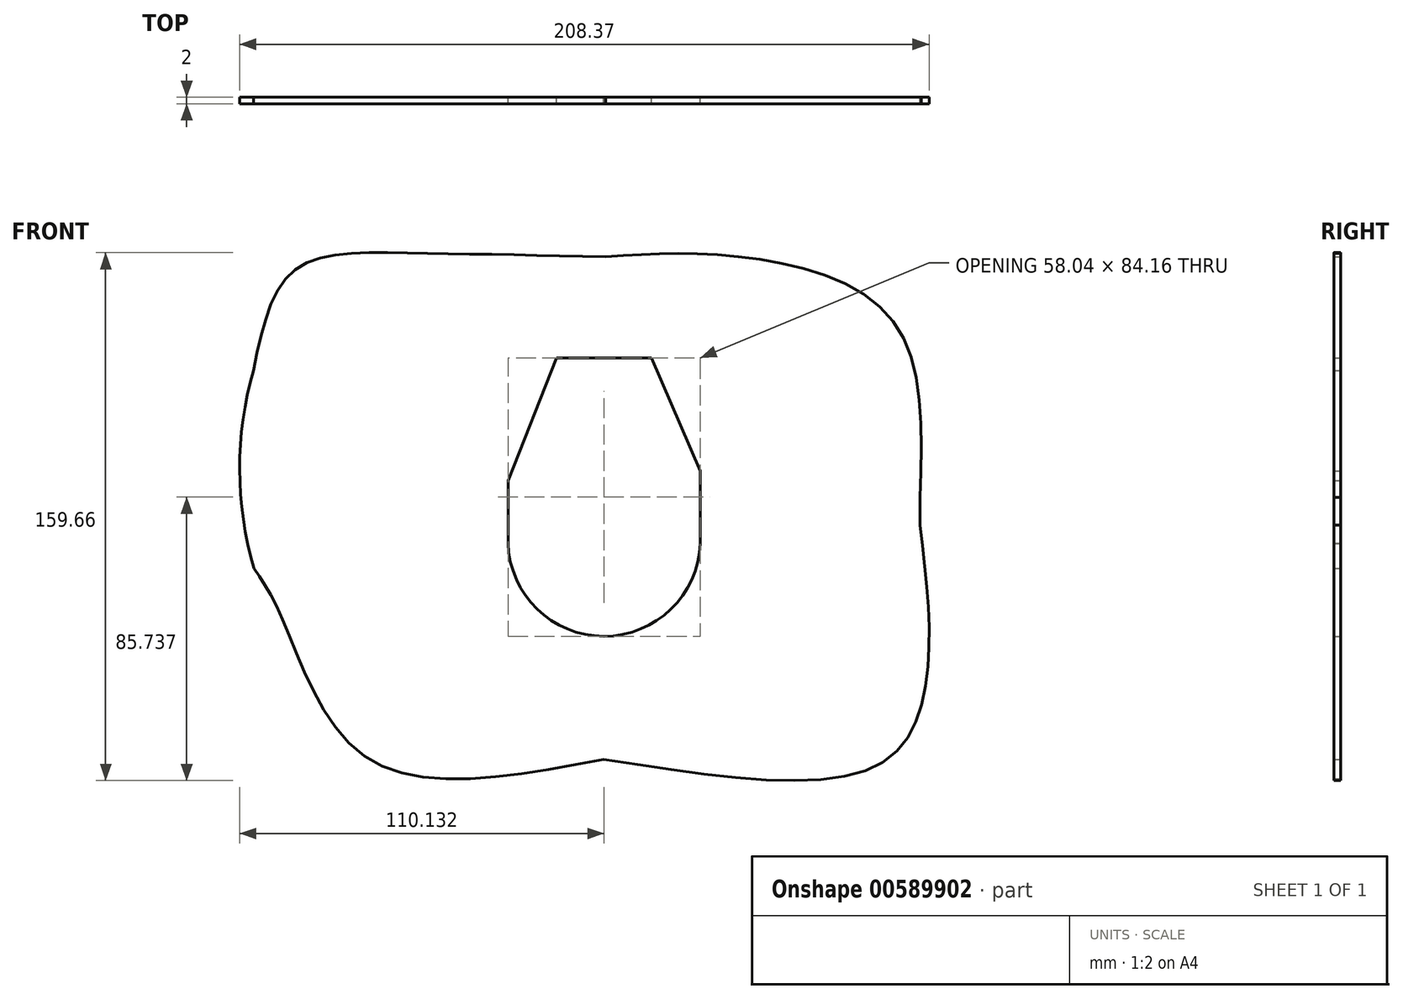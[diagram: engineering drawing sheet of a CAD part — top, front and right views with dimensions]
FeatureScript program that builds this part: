
annotation { "Feature Type Name" : "Feature", "Feature Type Description" : "" }
export const myFeature = defineFeature(function(context is Context, id is Id, definition is map)
    precondition{}
    {
        {
            var Q0;
            Q0=qCreatedBy(makeId("Front.planeOp"),FACE);
            var sketch = newSketch(context, id + "F0", { "sketchPlane" : qUnion([Q0])});
            skFitSpline(sketch, "E0.0", {"points": [v(-142.2, 80.43) * mm, v(-130.3, 110.35) * mm, v(-98.28, 116.01) * mm, v(-35.75, 114.87) * mm]});
            skFitSpline(sketch, "E1.0", {"points": [v(-35.75, 114.87) * mm, v(4.23, 114.9) * mm, v(50.43, 96.27) * mm, v(59.22, 42.04) * mm]});
            skFitSpline(sketch, "E2.0", {"points": [v(-36.38, -37.12) * mm, v(47.08, -38.61) * mm, v(61.61, -9.55) * mm, v(59.22, 33.68) * mm]});
            skFitSpline(sketch, "E3.0", {"points": [v(-36.38, -37.12) * mm, v(-108.3, -36.38) * mm, v(-133.63, 5.73) * mm, v(-142.09, 20.66) * mm]});
            skLineSegment(sketch, "E4.0", {"start": v(-50.58, 84.24) * mm, "end": v(-21.86, 84.24) * mm});
            skLineSegment(sketch, "E5.0", {"start": v(-65.24, 47.19) * mm, "end": v(-50.58, 84.24) * mm});
            skLineSegment(sketch, "E6.0", {"start": v(-65.24, 47.19) * mm, "end": v(-65.24, 28.24) * mm});
            skArc(sketch, "E7.0", {"start": v(-65.24, 28.24) * mm, "mid": v(-36.26, 0.08) * mm, "end": v(-7.2, 28.16) * mm});
            skLineSegment(sketch, "E8.0", {"start": v(-7.2, 50.02) * mm, "end": v(-7.2, 28.16) * mm});
            skLineSegment(sketch, "E9.0", {"start": v(-21.86, 84.24) * mm, "end": v(-7.2, 50.02) * mm});
            skArc(sketch, "E10", {"start": v(-142.2, 80.43) * mm, "mid": v(-146.35, 50.54) * mm, "end": v(-142.09, 20.66) * mm});
            skLineSegment(sketch, "E11", {"start": v(59.22, 42.04) * mm, "end": v(59.22, 33.68) * mm});
            skLineSegment(sketch, "E12", {"start": v(-124.67, -3.18) * mm, "end": v(-124.67, 67) * mm});
            skLineSegment(sketch, "E13", {"start": v(-124.67, 67) * mm, "end": v(-108.79, 67) * mm});
            skLineSegment(sketch, "E14", {"start": v(-108.79, 67) * mm, "end": v(-108.79, -16.62) * mm});
            skSolve(sketch);
        }
        {
            var Q0;
            {var subQ0=sQuery(id+"F0.wireOp",EDGE,"E12");Q0=makeQuery(id+"F0.imprint","IMPRINT",FACE,{"disambiguationData":[TD([[makeQuery(id+"F0.imprint","IMPRINT",EDGE,{"derivedFrom":subQ0}),-1.0]])]});}
            var Q1;
            Q1=makeQuery(id+"F0.imprint","IMPRINT",FACE,{"disambiguationData":[TD([[makeQuery(id+"F0.imprint","IMPRINT",EDGE,{"derivedFrom":sQuery(id+"F0.wireOp",EDGE,"E0.0")}),-1.0]])]});
            extrude(context, id + "F1", {"entities" : qUnion([Q0, Q1]), "depth" : 2 * mm, "offsetDistance" : 25 * mm});
        }
    });
